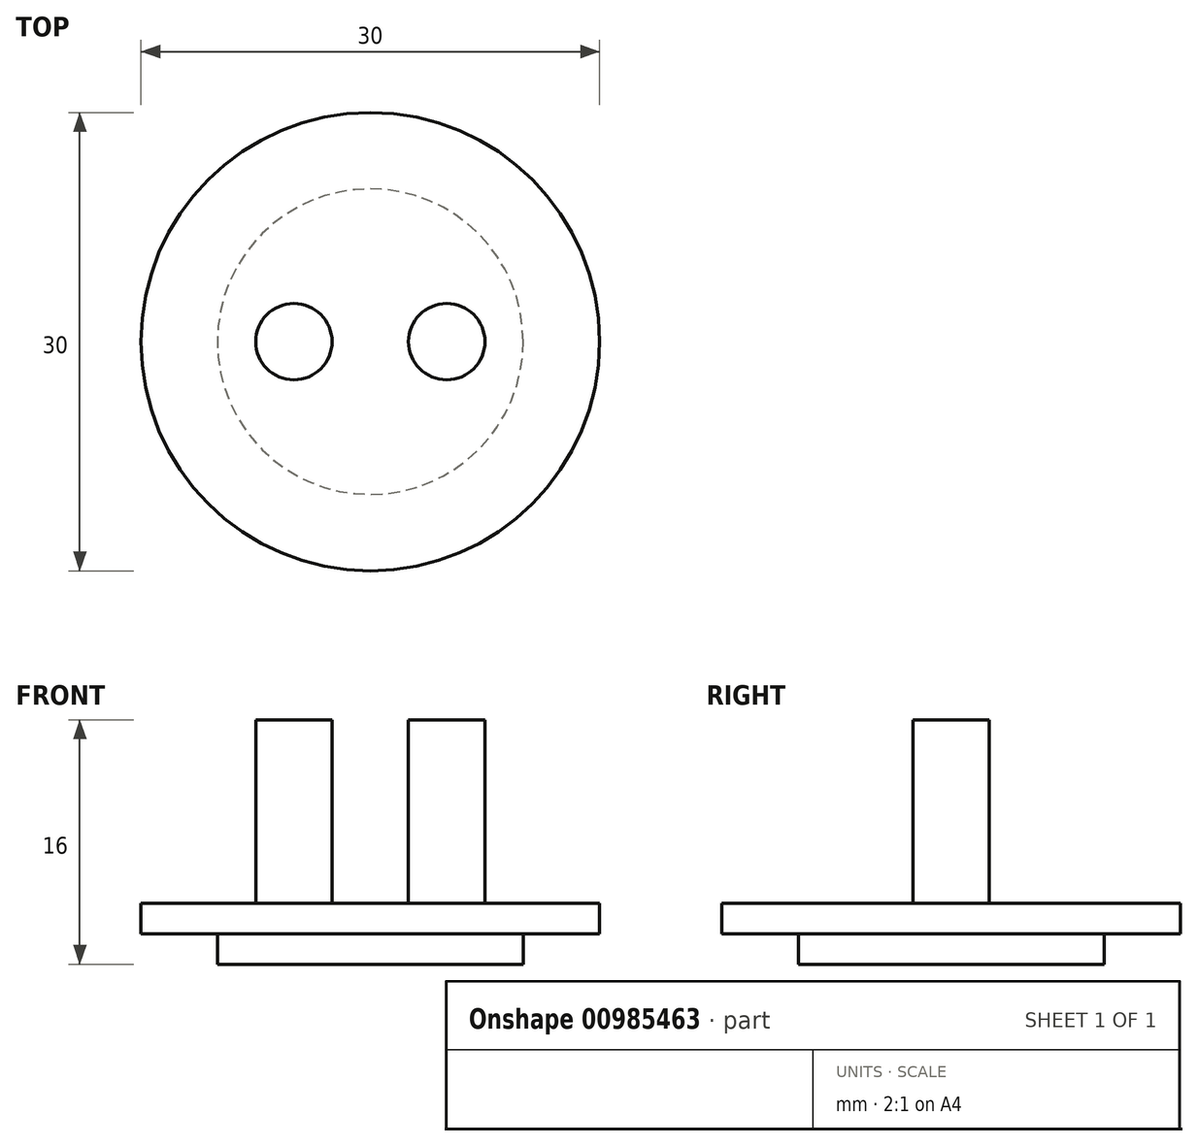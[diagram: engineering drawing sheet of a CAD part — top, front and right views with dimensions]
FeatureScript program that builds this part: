
annotation { "Feature Type Name" : "Feature", "Feature Type Description" : "" }
export const myFeature = defineFeature(function(context is Context, id is Id, definition is map)
    precondition{}
    {
        {
            var Q0;
            Q0=qCreatedBy(makeId("Top.planeOp"),FACE);
            var sketch = newSketch(context, id + "F0", { "sketchPlane" : qUnion([Q0])});
            skCircle(sketch, "E0", {"center": v(0, 0) * mm, "radius": 10 * mm});
            skSolve(sketch);
        }
        {
            var Q0;
            Q0=makeQuery(id+"F0.imprint","IMPRINT",FACE,{"disambiguationData":[TD([[makeQuery(id+"F0.imprint","IMPRINT",EDGE,{"derivedFrom":sQuery(id+"F0.wireOp",EDGE,"E0")}),1.0]])]});
            extrude(context, id + "F1", {"entities" : qUnion([Q0]), "depth" : 2 * mm, "offsetDistance" : 25 * mm});
        }
        {
            var Q0;
            Q0=makeQuery(id+"F1.opExtrude","CAP_FACE",FACE,{"disambiguationData":[OSD([sQuery(id+"F0.wireOp",EDGE,"E0")])],"isStart":false});
            var sketch = newSketch(context, id + "F2", { "sketchPlane" : qUnion([Q0])});
            skCircle(sketch, "E1", {"center": v(0, 0) * mm, "radius": 15 * mm});
            skSolve(sketch);
        }
        {
            var Q0;
            Q0=qSketchRegion(id+"F2",true);
            extrude(context, id + "F3", {"entities" : qUnion([Q0]), "operationType" : NewBodyOperationType.ADD, "depth" : 2 * mm, "offsetDistance" : 25 * mm});
        }
        {
            var Q0;
            Q0=makeQuery(id+"F3.opExtrude","CAP_FACE",FACE,{"disambiguationData":[OSD([sQuery(id+"F2.wireOp",EDGE,"E1")])],"isStart":false});
            var sketch = newSketch(context, id + "F4", { "sketchPlane" : qUnion([Q0])});
            skLineSegment(sketch, "E2", {"start": v(-15, 0) * mm, "end": v(15, 0) * mm, "construction": true});
            skCircle(sketch, "E3", {"center": v(-5, 0) * mm, "radius": 2.5 * mm});
            skCircle(sketch, "E4.MirrorC", {"center": v(5, 0) * mm, "radius": 2.5 * mm});
            skSolve(sketch);
        }
        {
            var Q0;
            Q0 = qSketchRegion(id + "F4", true);
            extrude(context, id + "F5", {"entities" : qUnion([Q0]), "operationType" : NewBodyOperationType.ADD, "depth" : 12 * mm, "offsetDistance" : 25 * mm});
        }
    });
